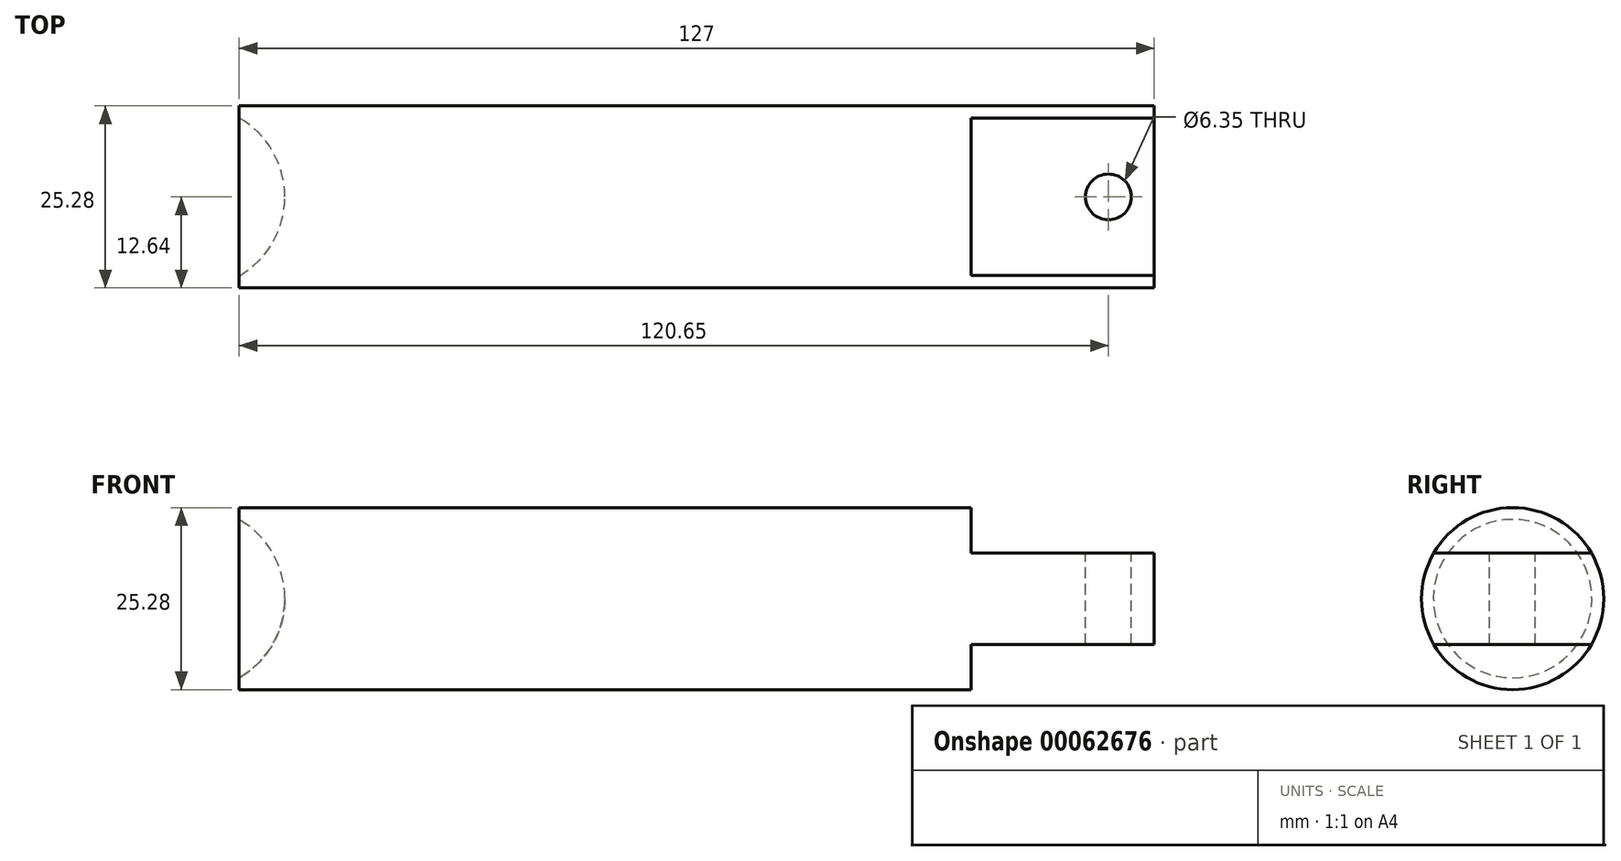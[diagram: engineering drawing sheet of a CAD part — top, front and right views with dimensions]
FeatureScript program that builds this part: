
annotation { "Feature Type Name" : "Feature", "Feature Type Description" : "" }
export const myFeature = defineFeature(function(context is Context, id is Id, definition is map)
    precondition{}
    {
        {
            var Q0;
            Q0=qCreatedBy(makeId("Front.planeOp"),FACE);
            var sketch = newSketch(context, id + "F0", { "sketchPlane" : qUnion([Q0])});
            skLineSegment(sketch, "E0.bottom", {"start": v(6.35, 0) * mm, "end": v(127, 0) * mm});
            skLineSegment(sketch, "E0.top", {"start": v(0, 12.64) * mm, "end": v(127, 12.64) * mm});
            skLineSegment(sketch, "E0.left", {"start": v(0, 11) * mm, "end": v(0, 12.64) * mm});
            skLineSegment(sketch, "E0.right", {"start": v(127, 0) * mm, "end": v(127, 12.64) * mm});
            skArc(sketch, "E1", {"start": v(6.35, 0) * mm, "mid": v(4.65, 6.35) * mm, "end": v(0, 11) * mm});
            skPoint(sketch, "E2.orphan", {"position": v(0, 0) * mm});
            skSolve(sketch);
        }
        {
            var Q0;
            Q0=makeQuery(id+"F0.imprint","IMPRINT",FACE,{"disambiguationData":[TD([[makeQuery(id+"F0.imprint","IMPRINT",EDGE,{"derivedFrom":sQuery(id+"F0.wireOp",EDGE,"E0.bottom")}),1.0]])]});
            var Q1;
            Q1=sQuery(id+"F0.wireOp",EDGE,"E0.bottom");
            revolve(context, id + "F1", {"entities" : qUnion([Q0]), "axis" : qUnion([Q1]), "revolveType" : RevolveType.FULL});
        }
        {
            var Q0;
            Q0=qCreatedBy(makeId("Front.planeOp"),FACE);
            var sketch = newSketch(context, id + "F2", { "sketchPlane" : qUnion([Q0])});
            skLineSegment(sketch, "E3.bottom", {"start": v(101.6, 23.62) * mm, "end": v(143.08, 23.62) * mm});
            skLineSegment(sketch, "E3.top", {"start": v(101.6, 6.35) * mm, "end": v(143.08, 6.35) * mm});
            skLineSegment(sketch, "E3.left", {"start": v(101.6, 23.62) * mm, "end": v(101.6, 6.35) * mm});
            skLineSegment(sketch, "E3.right", {"start": v(143.08, 23.62) * mm, "end": v(143.08, 6.35) * mm});
            skLineSegment(sketch, "E4.bottom", {"start": v(101.6, -6.35) * mm, "end": v(143.84, -6.35) * mm});
            skLineSegment(sketch, "E4.top", {"start": v(101.6, -20.88) * mm, "end": v(143.84, -20.88) * mm});
            skLineSegment(sketch, "E4.left", {"start": v(101.6, -6.35) * mm, "end": v(101.6, -20.88) * mm});
            skLineSegment(sketch, "E4.right", {"start": v(143.84, -6.35) * mm, "end": v(143.84, -20.88) * mm});
            skSolve(sketch);
        }
        {
            var Q0;
            Q0=makeQuery(id+"F2.imprint","IMPRINT",FACE,{"disambiguationData":[TD([[makeQuery(id+"F2.imprint","IMPRINT",EDGE,{"derivedFrom":sQuery(id+"F2.wireOp",EDGE,"E3.bottom")}),-1.0]])]});
            var Q1;
            Q1=makeQuery(id+"F2.imprint","IMPRINT",FACE,{"disambiguationData":[TD([[makeQuery(id+"F2.imprint","IMPRINT",EDGE,{"derivedFrom":sQuery(id+"F2.wireOp",EDGE,"E4.bottom")}),-1.0]])]});
            extrude(context, id + "F3", {"entities" : qUnion([Q0, Q1]), "operationType" : NewBodyOperationType.REMOVE, "endBound" : BoundingType.THROUGH_ALL, "oppositeDirection" : true, "depth" : 25.4 * mm, "hasSecondDirection" : true, "secondDirectionOppositeDirection" : false, "secondDirectionDepth" : 25.4 * mm});
        }
        {
            var Q0;
            Q0=makeQuery(id+"F3.boolean.opBoolean","COPY",FACE,{"derivedFrom":makeQuery(id+"F3.opExtrude","SWEPT_FACE",FACE,{"disambiguationData":[OSD([sQuery(id+"F2.wireOp",EDGE,"E4.bottom")])]})});
            var sketch = newSketch(context, id + "F4", { "sketchPlane" : qUnion([Q0])});
            skCircle(sketch, "E5", {"center": v(120.65, 0) * mm, "radius": 3.18 * mm});
            skSolve(sketch);
        }
        {
            var Q0;
            Q0=sQuery(id+"F4.wireOp",VERTEX,"E5.center");
            var Q1;
            Q1=makeQuery(id+"F1.opRevolve","SWEPT_BODY",BODY,{"disambiguationData":[OSD([sQuery(id+"F0.wireOp",EDGE,"E0.bottom"),sQuery(id+"F0.wireOp",EDGE,"E0.top"),sQuery(id+"F0.wireOp",EDGE,"E0.left"),sQuery(id+"F0.wireOp",EDGE,"E0.right"),sQuery(id+"F0.wireOp",EDGE,"E1")])]});
            hole(context, id + "F5", {"style" : HoleStyle.SIMPLE, "holeDiameter" : 6.35 * mm, "endStyle" : HoleEndStyle.THROUGH, "locations" : qUnion([Q0]), "scope" : qUnion([Q1])});
        }
    });
